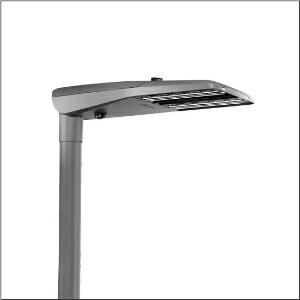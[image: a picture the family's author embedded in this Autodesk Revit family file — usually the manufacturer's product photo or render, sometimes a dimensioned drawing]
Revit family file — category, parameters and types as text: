
# Revit family: streetlight_sl_11_iq_midi___st1_2a_5xc3a41y08me_bddd
name_source: partatom
category: Lighting Fixtures
units: mm (PartAtom-declared; Revit-internal decimal feet)

## family parameters
Cut with Voids When Loaded = No
Host = Face
Light Source = No
Part Type = Normal
Room Calculation Point = No
Round Connector Dimension = Use Diameter
Shared = No

## types (1)
- --- (1 x LED, 18900 lm, 122.6 W, 4000K)
    Apparent Load = 123 VA
    CIE Flux Codes = 32 70 96 100 100
    Color Rendering = 70
    Color Temperature = 4000K
    Default Elevation = 1800 mm
    Description = Streetlight SL 11 iQ midi, mast luminaire, primary light control with 3 zone facetted reflector, of plastic, silver coated, highly specular, primary optical cover: cover, of PMMA, transparent, light distribution: ST1.2a, light emission: direct distribution, primary light characteristic: asymmetric, installation type: post-top, side-entry, LED, High Power LED, rated luminous flux: 18.900lm, luminous efficacy: 154lm/W, light colour: 740, colour temperature: 4000K, control: presetting dimming logarithmic, Street-Remote, Auto-Match, Temp-Guard, Lumen-Switch, Night-Set, Smart-Wire, Light-Fading, Desk-Remote (wireless, voltage-free reading and setting of iQ features in the workshop via application-optimized NFC function/RFID function), optimised constant luminous flux control (CLO 2.0), with cable H07RN-F 5x 1.5mm², mains connection: 230..240V, AC, 50/60Hz, connection cable pre-assembled, cable length: 12,5m, start of lifetime: 123W, end of service life: 130W, reduction: 56W, luminaire housing, of diecast aluminium, powder-coated, Siteco® metallic grey (DB 702S), please order mast flange separately, inclination adjustable without tools: 0°, 5°, 10°, 15° (post-top) | 0°, -5°, -10°, -15° (side-entry), sealing non-destructively replaceable, multi-level sealing system, length: 780mm, width: 376mm, height: 118mm, mast flange for spigot size: 42mm (side-entry): 5XC10008XM4, 60/48mm (side-entry/post-top): 5XC10108XM2, 76/60mm (side-entry/post-top): 5XC10108XM1, equipment: Power, Smart Interface below and above, protection rating (complete): IP66, insulation class (complete): insulation class II (safety insulation), certification: CE, ENEC, VDE, UKCA, impact resistance: IK09, permissible operating ambient temperature for outdoor applications: -25..+50°C, standard-compliant lighting for roads and squares, Environmental Product Declaration (EPD) tested and certified by an independent institute, packaging unit: 1 piece

Light Distribution: ST1.2a
    Height = 118 mm
    Lamp = 1 x LED
    Lamp Light Flux = 18900 lm
    Lamp Power = 122.6 W
    Lamp count = 1
    Length = 780 mm
    Luminous efficacy = 154 lm/W
    Manufacturer = Siteco
    ModVariant = No
    Model = 5XC3A41Y08ME
    Number of Poles = 1
    OnlyDefault = Yes
    Power Factor = 1
    Product Name = Streetlight SL 11 iQ midi | ST1.2a
    Product group = mast luminaire | pylon top
    ProductGroupID = 6100
    Protection Class = Protection class II
    Protection Degree = IP 66
    RLX_Detail_Level = 1
    RLX_Emergency_Light_Flux = 0 lm
    RLX_Emergency_Type = 0
    RLX_Emergency_Type_DB = No
    RlxData = <blob elided: 69629 chars, md5=33c0fd50>
    Socket = socket
    Standby Power = 0 W
    System Light Flux = 18900 lm
    System Power = 123 W
    Type Comments = factory setting: luminous flux: 100 % | dim-lin: 254 | 552 mA
    Type Image = l_1004429.jpg
    URL = http://relux.com
    VarID = @adj_082529
    Voltage = 0 V
    Weight = 0.00 kg
    Width = 376 mm

## geometry (parser evidence)
native form markers: Blend x4, Sweep x8
no freeform markers — native parametric forms only
